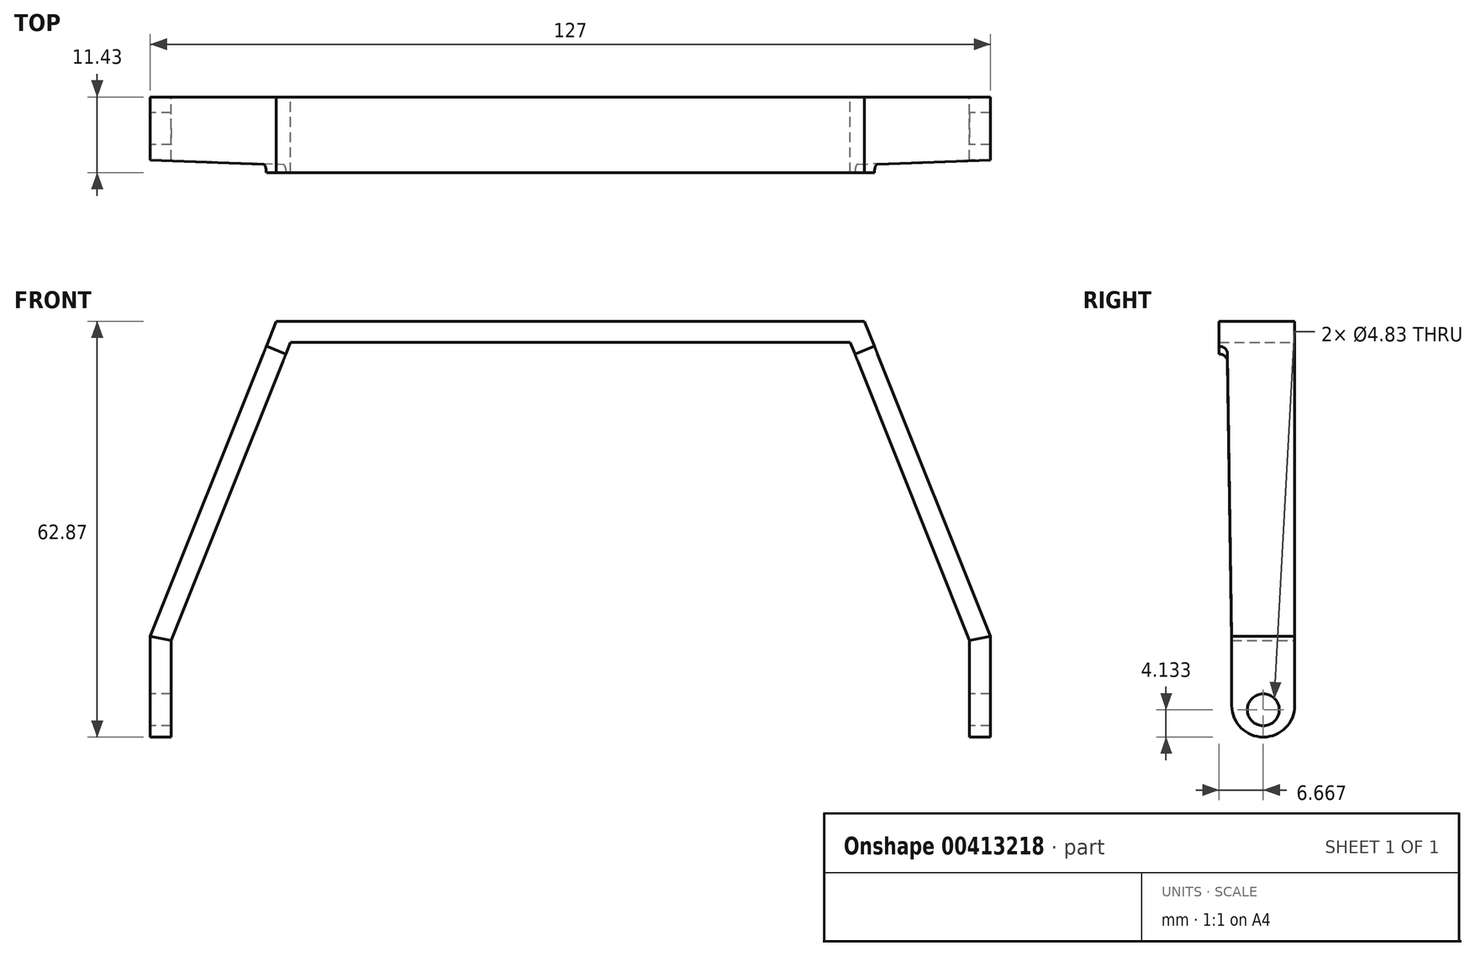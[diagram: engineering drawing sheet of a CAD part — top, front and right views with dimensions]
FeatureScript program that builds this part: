
annotation { "Feature Type Name" : "Feature", "Feature Type Description" : "" }
export const myFeature = defineFeature(function(context is Context, id is Id, definition is map)
    precondition{}
    {
        {
            var Q0;
            Q0=qCreatedBy(makeId("Front.planeOp"),FACE);
            var sketch = newSketch(context, id + "F0", { "sketchPlane" : qUnion([Q0])});
            skLineSegment(sketch, "E0.bottom", {"start": v(107.95, 63.5) * mm, "end": v(19.05, 63.5) * mm});
            skLineSegment(sketch, "E0.left", {"start": v(127, 15.87) * mm, "end": v(127, 0) * mm});
            skLineSegment(sketch, "E0.right", {"start": v(0, 15.87) * mm, "end": v(0, 0) * mm});
            skLineSegment(sketch, "E1", {"start": v(0, 15.87) * mm, "end": v(19.05, 63.5) * mm});
            skLineSegment(sketch, "E2", {"start": v(107.95, 63.5) * mm, "end": v(127, 15.87) * mm});
            skLineSegment(sketch, "E3", {"start": v(21.2, 60.32) * mm, "end": v(3.17, 15.26) * mm});
            skLineSegment(sketch, "E4", {"start": v(105.8, 60.32) * mm, "end": v(123.82, 15.26) * mm});
            skLineSegment(sketch, "E5", {"start": v(0, 0.63) * mm, "end": v(3.17, 0.63) * mm});
            skLineSegment(sketch, "E6.trimOffspring", {"start": v(123.82, 0.63) * mm, "end": v(127, 0.63) * mm});
            skLineSegment(sketch, "E7.trimOffspring", {"start": v(105.8, 60.32) * mm, "end": v(21.2, 60.32) * mm});
            skLineSegment(sketch, "E8.trimOffspring", {"start": v(3.17, 15.26) * mm, "end": v(3.17, 0) * mm});
            skLineSegment(sketch, "E9.trimOffspring", {"start": v(123.82, 15.26) * mm, "end": v(123.82, 0) * mm});
            skSolve(sketch);
        }
        {
            var Q0;
            Q0=makeQuery(id+"F0.imprint","IMPRINT",FACE,{"disambiguationData":[TD([[makeQuery(id+"F0.imprint","IMPRINT",EDGE,{"derivedFrom":sQuery(id+"F0.wireOp",EDGE,"E0.bottom")}),1.0]])]});
            extrude(context, id + "F1", {"entities" : qUnion([Q0]), "depth" : 9.52 * mm});
        }
        {
            var Q0;
            Q0=makeQuery(id+"F1.opExtrude","SWEPT_FACE",FACE,{"disambiguationData":[OSD([sQuery(id+"F0.wireOp",EDGE,"E0.right")])]});
            var sketch = newSketch(context, id + "F2", { "sketchPlane" : qUnion([Q0])});
            skCircle(sketch, "E10", {"center": v(4.76, 4.76) * mm, "radius": 2.41 * mm});
            skPoint(sketch, "E10.centerSnap0", {"position": v(4.76, 0.63) * mm});
            skSolve(sketch);
        }
        {
            var Q0;
            Q0=makeQuery(id+"F2.imprint","IMPRINT",FACE,{"disambiguationData":[TD([[makeQuery(id+"F2.imprint","IMPRINT",EDGE,{"derivedFrom":sQuery(id+"F2.wireOp",EDGE,"E10")}),1.0]])]});
            extrude(context, id + "F3", {"entities" : qUnion([Q0]), "operationType" : NewBodyOperationType.REMOVE, "endBound" : BoundingType.THROUGH_ALL, "oppositeDirection" : true, "depth" : 25.4 * mm});
        }
        {
            var Q0;
            Q0=makeQuery(id+"F1.opExtrude","CAP_EDGE",EDGE,{"disambiguationData":[OSD([sQuery(id+"F0.wireOp",EDGE,"E5")])],"isStart":false});
            var Q1;
            Q1=makeQuery(id+"F1.opExtrude","CAP_EDGE",EDGE,{"disambiguationData":[OSD([sQuery(id+"F0.wireOp",EDGE,"E5")])],"isStart":true});
            var Q2;
            Q2=makeQuery(id+"F1.opExtrude","CAP_EDGE",EDGE,{"disambiguationData":[OSD([sQuery(id+"F0.wireOp",EDGE,"E6.trimOffspring")])],"isStart":false});
            var Q3;
            Q3=makeQuery(id+"F1.opExtrude","CAP_EDGE",EDGE,{"disambiguationData":[OSD([sQuery(id+"F0.wireOp",EDGE,"E6.trimOffspring")])],"isStart":true});
            fillet(context, id + "F4", {"entities" : qUnion([Q0, Q1, Q2, Q3]), "radius" : 4.76 * mm, "tangentPropagation" : true, "allowEdgeOverflow" : false});
        }
        {
            var Q0;
            Q0=makeQuery(id+"F1.opExtrude","CAP_FACE",FACE,{"disambiguationData":[OSD([sQuery(id+"F0.wireOp",EDGE,"E0.bottom"),sQuery(id+"F0.wireOp",EDGE,"E0.left"),sQuery(id+"F0.wireOp",EDGE,"E0.right"),sQuery(id+"F0.wireOp",EDGE,"E1"),sQuery(id+"F0.wireOp",EDGE,"E2"),sQuery(id+"F0.wireOp",EDGE,"E3"),sQuery(id+"F0.wireOp",EDGE,"E4"),sQuery(id+"F0.wireOp",EDGE,"E5"),sQuery(id+"F0.wireOp",EDGE,"E6.trimOffspring"),sQuery(id+"F0.wireOp",EDGE,"E7.trimOffspring"),sQuery(id+"F0.wireOp",EDGE,"E8.trimOffspring"),sQuery(id+"F0.wireOp",EDGE,"E9.trimOffspring")])],"isStart":false});
            var sketch = newSketch(context, id + "F5", { "sketchPlane" : qUnion([Q0])});
            skLineSegment(sketch, "E11", {"start": v(105.8, 60.32) * mm, "end": v(123.82, 15.26) * mm});
            skLineSegment(sketch, "E12", {"start": v(123.82, 15.26) * mm, "end": v(127, 15.87) * mm});
            skLineSegment(sketch, "E13", {"start": v(127, 15.87) * mm, "end": v(107.95, 63.5) * mm});
            skLineSegment(sketch, "E14", {"start": v(107.95, 63.5) * mm, "end": v(19.05, 63.5) * mm});
            skLineSegment(sketch, "E15", {"start": v(19.05, 63.5) * mm, "end": v(0, 15.87) * mm});
            skLineSegment(sketch, "E16", {"start": v(0, 15.87) * mm, "end": v(3.17, 15.26) * mm});
            skLineSegment(sketch, "E17", {"start": v(3.17, 15.26) * mm, "end": v(21.2, 60.32) * mm});
            skLineSegment(sketch, "E18", {"start": v(21.2, 60.32) * mm, "end": v(105.8, 60.32) * mm});
            skSolve(sketch);
        }
        {
            var Q0;
            Q0=makeQuery(id+"F5.imprint","IMPRINT",FACE,{"disambiguationData":[TD([[makeQuery(id+"F5.imprint","IMPRINT",EDGE,{"derivedFrom":sQuery(id+"F5.wireOp",EDGE,"E11")}),1.0]])]});
            extrude(context, id + "F6", {"entities" : qUnion([Q0]), "operationType" : NewBodyOperationType.ADD, "depth" : 1.9 * mm});
        }
        {
            var Q0;
            Q0=makeQuery(id+"F6.boolean.opBoolean","MERGE",FACE,{"derivedFrom":[makeQuery(id+"F1.opExtrude","SWEPT_FACE",FACE,{"disambiguationData":[OSD([sQuery(id+"F0.wireOp",EDGE,"E2")])]}),makeQuery(id+"F6.opExtrude","SWEPT_FACE",FACE,{"disambiguationData":[OSD([sQuery(id+"F5.wireOp",EDGE,"E13")])]})]});
            var sketch = newSketch(context, id + "F7", { "sketchPlane" : qUnion([Q0])});
            skCircle(sketch, "E19", {"center": v(-11.43, 13.54) * mm, "radius": 1.27 * mm});
            skLineSegment(sketch, "E20", {"start": v(-9.53, -32.43) * mm, "end": v(-10.2, 16.01) * mm});
            skLineSegment(sketch, "E21", {"start": v(-11.43, 12.27) * mm, "end": v(-11.43, -32.43) * mm});
            skLineSegment(sketch, "E22", {"start": v(-11.43, -32.43) * mm, "end": v(-9.53, -32.43) * mm});
            skSolve(sketch);
        }
        {
            var Q0;
            {var subQ0=sQuery(id+"F7.wireOp",EDGE,"E21");Q0=makeQuery(id+"F7.imprint","IMPRINT",FACE,{"disambiguationData":[TD([[makeQuery(id+"F7.imprint","IMPRINT",EDGE,{"derivedFrom":subQ0}),1.0]])]});}
            var Q1;
            {var subQ0=sQuery(id+"F7.wireOp",EDGE,"E20");var subQ1=sQuery(id+"F7.wireOp",EDGE,"E19");var subQ2=makeQuery(id+"F7.imprint","INTERSECT",VERTEX,{"disambiguationData":[OD(0.0)],"derivedFrom":[subQ1,subQ0]});Q1=makeQuery(id+"F7.imprint","IMPRINT",FACE,{"disambiguationData":[TD([[makeQuery(id+"F7.imprint","IMPRINT",EDGE,{"disambiguationData":[TD([[subQ2,1.0]])],"derivedFrom":subQ1}),1.0]])]});}
            var Q2;
            Q2=makeQuery(id+"F6.boolean.opBoolean","MERGE",FACE,{"derivedFrom":[makeQuery(id+"F1.opExtrude","SWEPT_FACE",FACE,{"disambiguationData":[OSD([sQuery(id+"F0.wireOp",EDGE,"E4")])]}),makeQuery(id+"F6.opExtrude","SWEPT_FACE",FACE,{"disambiguationData":[OSD([sQuery(id+"F5.wireOp",EDGE,"E11")])]})]});
            extrude(context, id + "F8", {"entities" : qUnion([Q0, Q1]), "operationType" : NewBodyOperationType.REMOVE, "endBound" : BoundingType.UP_TO_SURFACE, "oppositeDirection" : true, "endBoundEntityFace" : qUnion([Q2]), "depth" : 25.4 * mm});
        }
        {
            var Q0;
            Q0=makeQuery(id+"F6.boolean.opBoolean","MERGE",FACE,{"derivedFrom":[makeQuery(id+"F1.opExtrude","SWEPT_FACE",FACE,{"disambiguationData":[OSD([sQuery(id+"F0.wireOp",EDGE,"E1")])]}),makeQuery(id+"F6.opExtrude","SWEPT_FACE",FACE,{"disambiguationData":[OSD([sQuery(id+"F5.wireOp",EDGE,"E15")])]})]});
            var sketch = newSketch(context, id + "F9", { "sketchPlane" : qUnion([Q0])});
            skCircle(sketch, "E23", {"center": v(11.43, 60.7) * mm, "radius": 1.27 * mm});
            skLineSegment(sketch, "E24", {"start": v(9.53, 14.74) * mm, "end": v(10.2, 63.32) * mm});
            skLineSegment(sketch, "E25", {"start": v(11.43, 59.44) * mm, "end": v(11.43, 14.74) * mm});
            skLineSegment(sketch, "E26", {"start": v(11.43, 14.74) * mm, "end": v(9.53, 14.74) * mm});
            skSolve(sketch);
        }
        {
            var Q0;
            {var subQ0=sQuery(id+"F9.wireOp",EDGE,"E25");Q0=makeQuery(id+"F9.imprint","IMPRINT",FACE,{"disambiguationData":[TD([[makeQuery(id+"F9.imprint","IMPRINT",EDGE,{"derivedFrom":subQ0}),1.0]])]});}
            var Q1;
            {var subQ0=sQuery(id+"F9.wireOp",EDGE,"E23");var subQ1=makeQuery(id+"F9.imprint","INTERSECT",VERTEX,{"derivedFrom":[subQ0,sQuery(id+"F9.wireOp",EDGE,"E24")]});Q1=makeQuery(id+"F9.imprint","IMPRINT",FACE,{"disambiguationData":[TD([[makeQuery(id+"F9.imprint","IMPRINT",EDGE,{"disambiguationData":[TD([[subQ1,1.0]])],"derivedFrom":subQ0}),1.0]])]});}
            var Q2;
            Q2=makeQuery(id+"F6.boolean.opBoolean","MERGE",FACE,{"derivedFrom":[makeQuery(id+"F1.opExtrude","SWEPT_FACE",FACE,{"disambiguationData":[OSD([sQuery(id+"F0.wireOp",EDGE,"E3")])]}),makeQuery(id+"F6.opExtrude","SWEPT_FACE",FACE,{"disambiguationData":[OSD([sQuery(id+"F5.wireOp",EDGE,"E17")])]})]});
            extrude(context, id + "F10", {"entities" : qUnion([Q0, Q1]), "operationType" : NewBodyOperationType.REMOVE, "endBound" : BoundingType.UP_TO_SURFACE, "oppositeDirection" : true, "endBoundEntityFace" : qUnion([Q2]), "depth" : 25.4 * mm});
        }
    });
